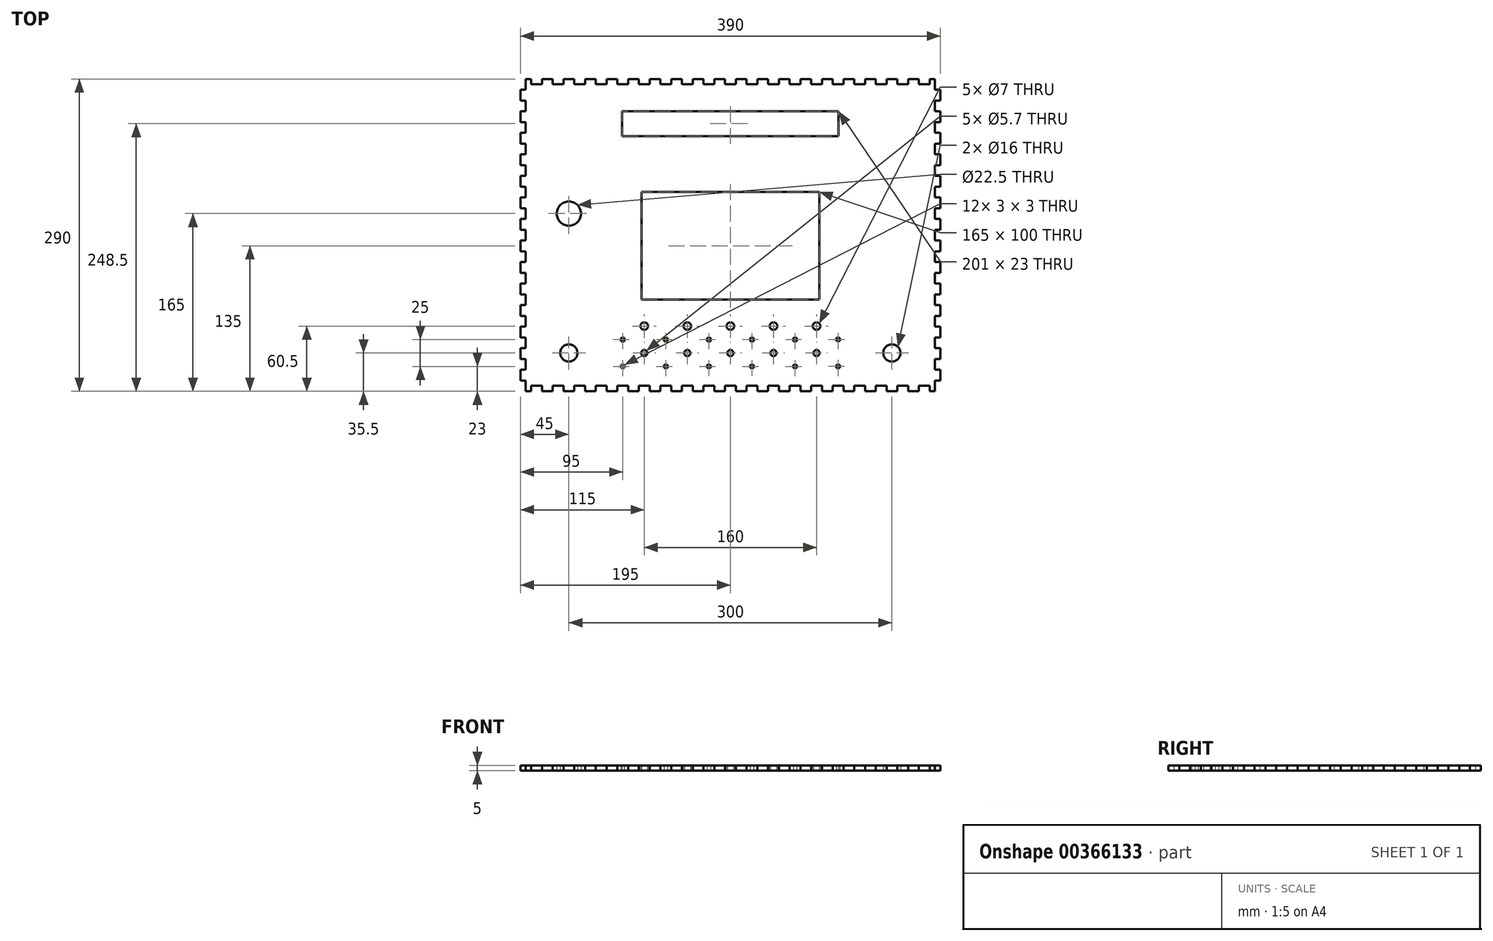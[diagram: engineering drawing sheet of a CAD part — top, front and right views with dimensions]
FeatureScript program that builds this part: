
annotation { "Feature Type Name" : "Feature", "Feature Type Description" : "" }
export const myFeature = defineFeature(function(context is Context, id is Id, definition is map)
    precondition{}
    {
        {
            var Q0;
            Q0=qCreatedBy(makeId("Top.planeOp"),FACE);
            var sketch = newSketch(context, id + "F0", { "sketchPlane" : qUnion([Q0])});
            skPoint(sketch, "E0.middle", {"position": v(0, 0) * mm});
            skLineSegment(sketch, "E1.bottom", {"start": v(82.5, -60) * mm, "end": v(-82.5, -60) * mm});
            skLineSegment(sketch, "E1.top", {"start": v(82.5, 40) * mm, "end": v(-82.5, 40) * mm});
            skLineSegment(sketch, "E1.left", {"start": v(82.5, -60) * mm, "end": v(82.5, 40) * mm});
            skLineSegment(sketch, "E1.right", {"start": v(-82.5, -60) * mm, "end": v(-82.5, 40) * mm});
            skPoint(sketch, "E1.middle", {"position": v(0, -10) * mm});
            skCircle(sketch, "E2", {"center": v(0, -84.5) * mm, "radius": 3.5 * mm});
            skCircle(sketch, "E3", {"center": v(40, -84.5) * mm, "radius": 3.5 * mm});
            skCircle(sketch, "E4", {"center": v(-80, -84.5) * mm, "radius": 3.5 * mm});
            skCircle(sketch, "E5", {"center": v(-40, -84.5) * mm, "radius": 3.5 * mm});
            skCircle(sketch, "E6", {"center": v(80, -84.5) * mm, "radius": 3.5 * mm});
            skLineSegment(sketch, "E7.bottom", {"start": v(100.5, 92) * mm, "end": v(-100.5, 92) * mm});
            skLineSegment(sketch, "E7.top", {"start": v(100.5, 115) * mm, "end": v(-100.5, 115) * mm});
            skLineSegment(sketch, "E7.left", {"start": v(100.5, 92) * mm, "end": v(100.5, 115) * mm});
            skLineSegment(sketch, "E7.right", {"start": v(-100.5, 92) * mm, "end": v(-100.5, 115) * mm});
            skPoint(sketch, "E7.middle", {"position": v(0, 103.5) * mm});
            skCircle(sketch, "E8", {"center": v(0, -109.5) * mm, "radius": 2.85 * mm});
            skCircle(sketch, "E9", {"center": v(-40, -109.5) * mm, "radius": 2.85 * mm});
            skCircle(sketch, "E10", {"center": v(-80, -109.5) * mm, "radius": 2.85 * mm});
            skCircle(sketch, "E11", {"center": v(40, -109.5) * mm, "radius": 2.85 * mm});
            skCircle(sketch, "E12", {"center": v(80, -109.5) * mm, "radius": 2.85 * mm});
            skCircle(sketch, "E13", {"center": v(-150, -109.5) * mm, "radius": 8 * mm});
            skCircle(sketch, "E14", {"center": v(150, -109.5) * mm, "radius": 8 * mm});
            skCircle(sketch, "E15", {"center": v(-150, 20) * mm, "radius": 11.25 * mm});
            skLineSegment(sketch, "E16.bottom", {"start": v(-18.5, -98.5) * mm, "end": v(-21.5, -98.5) * mm});
            skLineSegment(sketch, "E16.top", {"start": v(-18.5, -95.5) * mm, "end": v(-21.5, -95.5) * mm});
            skLineSegment(sketch, "E16.left", {"start": v(-18.5, -98.5) * mm, "end": v(-18.5, -95.5) * mm});
            skLineSegment(sketch, "E16.right", {"start": v(-21.5, -98.5) * mm, "end": v(-21.5, -95.5) * mm});
            skPoint(sketch, "E16.middle", {"position": v(-20, -97) * mm});
            skLineSegment(sketch, "E17.bottom", {"start": v(-58.5, -98.5) * mm, "end": v(-61.5, -98.5) * mm});
            skLineSegment(sketch, "E17.top", {"start": v(-58.5, -95.5) * mm, "end": v(-61.5, -95.5) * mm});
            skLineSegment(sketch, "E17.left", {"start": v(-58.5, -98.5) * mm, "end": v(-58.5, -95.5) * mm});
            skLineSegment(sketch, "E17.right", {"start": v(-61.5, -98.5) * mm, "end": v(-61.5, -95.5) * mm});
            skPoint(sketch, "E17.middle", {"position": v(-60, -97) * mm});
            skLineSegment(sketch, "E18.bottom", {"start": v(-98.5, -98.5) * mm, "end": v(-101.5, -98.5) * mm});
            skLineSegment(sketch, "E18.top", {"start": v(-98.5, -95.5) * mm, "end": v(-101.5, -95.5) * mm});
            skLineSegment(sketch, "E18.left", {"start": v(-98.5, -98.5) * mm, "end": v(-98.5, -95.5) * mm});
            skLineSegment(sketch, "E18.right", {"start": v(-101.5, -98.5) * mm, "end": v(-101.5, -95.5) * mm});
            skPoint(sketch, "E18.middle", {"position": v(-100, -97) * mm});
            skLineSegment(sketch, "E19.bottom", {"start": v(101.5, -98.39) * mm, "end": v(98.5, -98.39) * mm});
            skLineSegment(sketch, "E19.top", {"start": v(101.5, -95.39) * mm, "end": v(98.5, -95.39) * mm});
            skLineSegment(sketch, "E19.left", {"start": v(101.5, -98.39) * mm, "end": v(101.5, -95.39) * mm});
            skLineSegment(sketch, "E19.right", {"start": v(98.5, -98.39) * mm, "end": v(98.5, -95.39) * mm});
            skPoint(sketch, "E19.middle", {"position": v(100, -96.89) * mm});
            skLineSegment(sketch, "E20.bottom", {"start": v(61.5, -98.5) * mm, "end": v(58.5, -98.5) * mm});
            skLineSegment(sketch, "E20.top", {"start": v(61.5, -95.5) * mm, "end": v(58.5, -95.5) * mm});
            skLineSegment(sketch, "E20.left", {"start": v(61.5, -98.5) * mm, "end": v(61.5, -95.5) * mm});
            skLineSegment(sketch, "E20.right", {"start": v(58.5, -98.5) * mm, "end": v(58.5, -95.5) * mm});
            skPoint(sketch, "E20.middle", {"position": v(60, -97) * mm});
            skLineSegment(sketch, "E21.bottom", {"start": v(21.5, -98.5) * mm, "end": v(18.5, -98.5) * mm});
            skLineSegment(sketch, "E21.top", {"start": v(21.5, -95.5) * mm, "end": v(18.5, -95.5) * mm});
            skLineSegment(sketch, "E21.left", {"start": v(21.5, -98.5) * mm, "end": v(21.5, -95.5) * mm});
            skLineSegment(sketch, "E21.right", {"start": v(18.5, -98.5) * mm, "end": v(18.5, -95.5) * mm});
            skPoint(sketch, "E21.middle", {"position": v(20, -97) * mm});
            skPoint(sketch, "E22", {"position": v(-18.5, -97) * mm});
            skLineSegment(sketch, "E23.bottom", {"start": v(-18.5, -123.5) * mm, "end": v(-21.5, -123.5) * mm});
            skLineSegment(sketch, "E23.top", {"start": v(-18.5, -120.5) * mm, "end": v(-21.5, -120.5) * mm});
            skLineSegment(sketch, "E23.left", {"start": v(-18.5, -123.5) * mm, "end": v(-18.5, -120.5) * mm});
            skLineSegment(sketch, "E23.right", {"start": v(-21.5, -123.5) * mm, "end": v(-21.5, -120.5) * mm});
            skPoint(sketch, "E23.middle", {"position": v(-20, -122) * mm});
            skLineSegment(sketch, "E24.bottom", {"start": v(-58.5, -123.5) * mm, "end": v(-61.5, -123.5) * mm});
            skLineSegment(sketch, "E24.top", {"start": v(-58.5, -120.5) * mm, "end": v(-61.5, -120.5) * mm});
            skLineSegment(sketch, "E24.left", {"start": v(-58.5, -123.5) * mm, "end": v(-58.5, -120.5) * mm});
            skLineSegment(sketch, "E24.right", {"start": v(-61.5, -123.5) * mm, "end": v(-61.5, -120.5) * mm});
            skPoint(sketch, "E24.middle", {"position": v(-60, -122) * mm});
            skLineSegment(sketch, "E25.bottom", {"start": v(-98.5, -123.5) * mm, "end": v(-101.5, -123.5) * mm});
            skLineSegment(sketch, "E25.top", {"start": v(-98.5, -120.5) * mm, "end": v(-101.5, -120.5) * mm});
            skLineSegment(sketch, "E25.left", {"start": v(-98.5, -123.5) * mm, "end": v(-98.5, -120.5) * mm});
            skLineSegment(sketch, "E25.right", {"start": v(-101.5, -123.5) * mm, "end": v(-101.5, -120.5) * mm});
            skPoint(sketch, "E25.middle", {"position": v(-100, -122) * mm});
            skLineSegment(sketch, "E26.bottom", {"start": v(101.5, -123.39) * mm, "end": v(98.5, -123.39) * mm});
            skLineSegment(sketch, "E26.top", {"start": v(101.5, -120.39) * mm, "end": v(98.5, -120.39) * mm});
            skLineSegment(sketch, "E26.left", {"start": v(101.5, -123.39) * mm, "end": v(101.5, -120.39) * mm});
            skLineSegment(sketch, "E26.right", {"start": v(98.5, -123.39) * mm, "end": v(98.5, -120.39) * mm});
            skPoint(sketch, "E26.middle", {"position": v(100, -121.89) * mm});
            skLineSegment(sketch, "E27.bottom", {"start": v(61.5, -123.5) * mm, "end": v(58.5, -123.5) * mm});
            skLineSegment(sketch, "E27.top", {"start": v(61.5, -120.5) * mm, "end": v(58.5, -120.5) * mm});
            skLineSegment(sketch, "E27.left", {"start": v(61.5, -123.5) * mm, "end": v(61.5, -120.5) * mm});
            skLineSegment(sketch, "E27.right", {"start": v(58.5, -123.5) * mm, "end": v(58.5, -120.5) * mm});
            skPoint(sketch, "E27.middle", {"position": v(60, -122) * mm});
            skLineSegment(sketch, "E28.bottom", {"start": v(21.5, -123.5) * mm, "end": v(18.5, -123.5) * mm});
            skLineSegment(sketch, "E28.top", {"start": v(21.5, -120.5) * mm, "end": v(18.5, -120.5) * mm});
            skLineSegment(sketch, "E28.left", {"start": v(21.5, -123.5) * mm, "end": v(21.5, -120.5) * mm});
            skLineSegment(sketch, "E28.right", {"start": v(18.5, -123.5) * mm, "end": v(18.5, -120.5) * mm});
            skPoint(sketch, "E28.middle", {"position": v(20, -122) * mm});
            skPoint(sketch, "E29", {"position": v(-18.5, -122) * mm});
            skLineSegment(sketch, "E30", {"start": v(-195, -135) * mm, "end": v(-190, -135) * mm});
            skLineSegment(sketch, "E31", {"start": v(-190, -135) * mm, "end": v(-190, -145) * mm});
            skLineSegment(sketch, "E32", {"start": v(-190, -145) * mm, "end": v(-185, -145) * mm});
            skLineSegment(sketch, "E33", {"start": v(-185, -145) * mm, "end": v(-185, -140) * mm});
            skLineSegment(sketch, "E34", {"start": v(-185, -140) * mm, "end": v(-175, -140) * mm});
            skLineSegment(sketch, "E35", {"start": v(-175, -140) * mm, "end": v(-175, -145) * mm});
            skLineSegment(sketch, "E36", {"start": v(-175, -145) * mm, "end": v(-165, -145) * mm});
            skLineSegment(sketch, "E37", {"start": v(-165, -145) * mm, "end": v(-165, -140) * mm});
            skLineSegment(sketch, "E38", {"start": v(-165, -140) * mm, "end": v(-155, -140) * mm});
            skLineSegment(sketch, "E39", {"start": v(-155, -140) * mm, "end": v(-155, -145) * mm});
            skLineSegment(sketch, "E40.1.0.0", {"start": v(-155, -145) * mm, "end": v(-145, -145) * mm});
            skLineSegment(sketch, "E40.1.0.1", {"start": v(-145, -145) * mm, "end": v(-145, -140) * mm});
            skLineSegment(sketch, "E40.1.0.2", {"start": v(-145, -140) * mm, "end": v(-135, -140) * mm});
            skLineSegment(sketch, "E40.1.0.3", {"start": v(-135, -140) * mm, "end": v(-135, -145) * mm});
            skLineSegment(sketch, "E40.2.0.0", {"start": v(-135, -145) * mm, "end": v(-125, -145) * mm});
            skLineSegment(sketch, "E40.2.0.1", {"start": v(-125, -145) * mm, "end": v(-125, -140) * mm});
            skLineSegment(sketch, "E40.2.0.2", {"start": v(-125, -140) * mm, "end": v(-115, -140) * mm});
            skLineSegment(sketch, "E40.2.0.3", {"start": v(-115, -140) * mm, "end": v(-115, -145) * mm});
            skLineSegment(sketch, "E40.3.0.0", {"start": v(-115, -145) * mm, "end": v(-105, -145) * mm});
            skLineSegment(sketch, "E40.3.0.1", {"start": v(-105, -145) * mm, "end": v(-105, -140) * mm});
            skLineSegment(sketch, "E40.3.0.2", {"start": v(-105, -140) * mm, "end": v(-95, -140) * mm});
            skLineSegment(sketch, "E40.3.0.3", {"start": v(-95, -140) * mm, "end": v(-95, -145) * mm});
            skLineSegment(sketch, "E40.4.0.0", {"start": v(-95, -145) * mm, "end": v(-85, -145) * mm});
            skLineSegment(sketch, "E40.4.0.1", {"start": v(-85, -145) * mm, "end": v(-85, -140) * mm});
            skLineSegment(sketch, "E40.4.0.2", {"start": v(-85, -140) * mm, "end": v(-75, -140) * mm});
            skLineSegment(sketch, "E40.4.0.3", {"start": v(-75, -140) * mm, "end": v(-75, -145) * mm});
            skLineSegment(sketch, "E40.5.0.0", {"start": v(-75, -145) * mm, "end": v(-65, -145) * mm});
            skLineSegment(sketch, "E40.5.0.1", {"start": v(-65, -145) * mm, "end": v(-65, -140) * mm});
            skLineSegment(sketch, "E40.5.0.2", {"start": v(-65, -140) * mm, "end": v(-55, -140) * mm});
            skLineSegment(sketch, "E40.5.0.3", {"start": v(-55, -140) * mm, "end": v(-55, -145) * mm});
            skLineSegment(sketch, "E40.6.0.0", {"start": v(-55, -145) * mm, "end": v(-45, -145) * mm});
            skLineSegment(sketch, "E40.6.0.1", {"start": v(-45, -145) * mm, "end": v(-45, -140) * mm});
            skLineSegment(sketch, "E40.6.0.2", {"start": v(-45, -140) * mm, "end": v(-35, -140) * mm});
            skLineSegment(sketch, "E40.6.0.3", {"start": v(-35, -140) * mm, "end": v(-35, -145) * mm});
            skLineSegment(sketch, "E40.7.0.0", {"start": v(-35, -145) * mm, "end": v(-25, -145) * mm});
            skLineSegment(sketch, "E40.7.0.1", {"start": v(-25, -145) * mm, "end": v(-25, -140) * mm});
            skLineSegment(sketch, "E40.7.0.2", {"start": v(-25, -140) * mm, "end": v(-15, -140) * mm});
            skLineSegment(sketch, "E40.7.0.3", {"start": v(-15, -140) * mm, "end": v(-15, -145) * mm});
            skLineSegment(sketch, "E40.8.0.0", {"start": v(-15, -145) * mm, "end": v(-5, -145) * mm});
            skLineSegment(sketch, "E40.8.0.1", {"start": v(-5, -145) * mm, "end": v(-5, -140) * mm});
            skLineSegment(sketch, "E40.8.0.2", {"start": v(-5, -140) * mm, "end": v(5, -140) * mm});
            skLineSegment(sketch, "E40.8.0.3", {"start": v(5, -140) * mm, "end": v(5, -145) * mm});
            skLineSegment(sketch, "E40.9.0.0", {"start": v(5, -145) * mm, "end": v(15, -145) * mm});
            skLineSegment(sketch, "E40.9.0.1", {"start": v(15, -145) * mm, "end": v(15, -140) * mm});
            skLineSegment(sketch, "E40.9.0.2", {"start": v(15, -140) * mm, "end": v(25, -140) * mm});
            skLineSegment(sketch, "E40.9.0.3", {"start": v(25, -140) * mm, "end": v(25, -145) * mm});
            skLineSegment(sketch, "E40.10.0.0", {"start": v(25, -145) * mm, "end": v(35, -145) * mm});
            skLineSegment(sketch, "E40.10.0.1", {"start": v(35, -145) * mm, "end": v(35, -140) * mm});
            skLineSegment(sketch, "E40.10.0.2", {"start": v(35, -140) * mm, "end": v(45, -140) * mm});
            skLineSegment(sketch, "E40.10.0.3", {"start": v(45, -140) * mm, "end": v(45, -145) * mm});
            skLineSegment(sketch, "E40.11.0.0", {"start": v(45, -145) * mm, "end": v(55, -145) * mm});
            skLineSegment(sketch, "E40.11.0.1", {"start": v(55, -145) * mm, "end": v(55, -140) * mm});
            skLineSegment(sketch, "E40.11.0.2", {"start": v(55, -140) * mm, "end": v(65, -140) * mm});
            skLineSegment(sketch, "E40.11.0.3", {"start": v(65, -140) * mm, "end": v(65, -145) * mm});
            skLineSegment(sketch, "E40.12.0.0", {"start": v(65, -145) * mm, "end": v(75, -145) * mm});
            skLineSegment(sketch, "E40.12.0.1", {"start": v(75, -145) * mm, "end": v(75, -140) * mm});
            skLineSegment(sketch, "E40.12.0.2", {"start": v(75, -140) * mm, "end": v(85, -140) * mm});
            skLineSegment(sketch, "E40.12.0.3", {"start": v(85, -140) * mm, "end": v(85, -145) * mm});
            skLineSegment(sketch, "E40.13.0.0", {"start": v(85, -145) * mm, "end": v(95, -145) * mm});
            skLineSegment(sketch, "E40.13.0.1", {"start": v(95, -145) * mm, "end": v(95, -140) * mm});
            skLineSegment(sketch, "E40.13.0.2", {"start": v(95, -140) * mm, "end": v(105, -140) * mm});
            skLineSegment(sketch, "E40.13.0.3", {"start": v(105, -140) * mm, "end": v(105, -145) * mm});
            skLineSegment(sketch, "E40.14.0.0", {"start": v(105, -145) * mm, "end": v(115, -145) * mm});
            skLineSegment(sketch, "E40.14.0.1", {"start": v(115, -145) * mm, "end": v(115, -140) * mm});
            skLineSegment(sketch, "E40.14.0.2", {"start": v(115, -140) * mm, "end": v(125, -140) * mm});
            skLineSegment(sketch, "E40.14.0.3", {"start": v(125, -140) * mm, "end": v(125, -145) * mm});
            skLineSegment(sketch, "E40.15.0.0", {"start": v(125, -145) * mm, "end": v(135, -145) * mm});
            skLineSegment(sketch, "E40.15.0.1", {"start": v(135, -145) * mm, "end": v(135, -140) * mm});
            skLineSegment(sketch, "E40.15.0.2", {"start": v(135, -140) * mm, "end": v(145, -140) * mm});
            skLineSegment(sketch, "E40.15.0.3", {"start": v(145, -140) * mm, "end": v(145, -145) * mm});
            skLineSegment(sketch, "E40.16.0.0", {"start": v(145, -145) * mm, "end": v(155, -145) * mm});
            skLineSegment(sketch, "E40.16.0.1", {"start": v(155, -145) * mm, "end": v(155, -140) * mm});
            skLineSegment(sketch, "E40.16.0.2", {"start": v(155, -140) * mm, "end": v(165, -140) * mm});
            skLineSegment(sketch, "E40.16.0.3", {"start": v(165, -140) * mm, "end": v(165, -145) * mm});
            skLineSegment(sketch, "E40.17.0.0", {"start": v(165, -145) * mm, "end": v(175, -145) * mm});
            skLineSegment(sketch, "E40.17.0.1", {"start": v(175, -145) * mm, "end": v(175, -140) * mm});
            skLineSegment(sketch, "E40.17.0.2", {"start": v(175, -140) * mm, "end": v(185, -140) * mm});
            skLineSegment(sketch, "E40.17.0.3", {"start": v(185, -140) * mm, "end": v(185, -145) * mm});
            skLineSegment(sketch, "E40.direction1", {"start": v(-175, -145) * mm, "end": v(-155, -145) * mm, "construction": true});
            skLineSegment(sketch, "E41", {"start": v(185, -145) * mm, "end": v(190, -145) * mm});
            skLineSegment(sketch, "E42", {"start": v(190, -145) * mm, "end": v(190, -135) * mm});
            skLineSegment(sketch, "E43", {"start": v(190, -135) * mm, "end": v(195, -135) * mm});
            skLineSegment(sketch, "E44", {"start": v(195, 135) * mm, "end": v(190, 135) * mm});
            skLineSegment(sketch, "E45", {"start": v(190, 135) * mm, "end": v(190, 145) * mm});
            skLineSegment(sketch, "E46", {"start": v(190, 145) * mm, "end": v(185, 145) * mm});
            skLineSegment(sketch, "E47", {"start": v(185, 145) * mm, "end": v(185, 140) * mm});
            skLineSegment(sketch, "E48", {"start": v(185, 140) * mm, "end": v(175, 140) * mm});
            skLineSegment(sketch, "E49", {"start": v(175, 140) * mm, "end": v(175, 145) * mm});
            skLineSegment(sketch, "E50", {"start": v(175, 145) * mm, "end": v(165, 145) * mm});
            skLineSegment(sketch, "E51", {"start": v(165, 145) * mm, "end": v(165, 140) * mm});
            skLineSegment(sketch, "E52", {"start": v(165, 140) * mm, "end": v(155, 140) * mm});
            skLineSegment(sketch, "E53", {"start": v(155, 140) * mm, "end": v(155, 145) * mm});
            skLineSegment(sketch, "E54.1.0.0", {"start": v(155, 145) * mm, "end": v(145, 145) * mm});
            skLineSegment(sketch, "E54.1.0.1", {"start": v(145, 145) * mm, "end": v(145, 140) * mm});
            skLineSegment(sketch, "E54.1.0.2", {"start": v(145, 140) * mm, "end": v(135, 140) * mm});
            skLineSegment(sketch, "E54.1.0.3", {"start": v(135, 140) * mm, "end": v(135, 145) * mm});
            skLineSegment(sketch, "E54.2.0.0", {"start": v(135, 145) * mm, "end": v(125, 145) * mm});
            skLineSegment(sketch, "E54.2.0.1", {"start": v(125, 145) * mm, "end": v(125, 140) * mm});
            skLineSegment(sketch, "E54.2.0.2", {"start": v(125, 140) * mm, "end": v(115, 140) * mm});
            skLineSegment(sketch, "E54.2.0.3", {"start": v(115, 140) * mm, "end": v(115, 145) * mm});
            skLineSegment(sketch, "E54.3.0.0", {"start": v(115, 145) * mm, "end": v(105, 145) * mm});
            skLineSegment(sketch, "E54.3.0.1", {"start": v(105, 145) * mm, "end": v(105, 140) * mm});
            skLineSegment(sketch, "E54.3.0.2", {"start": v(105, 140) * mm, "end": v(95, 140) * mm});
            skLineSegment(sketch, "E54.3.0.3", {"start": v(95, 140) * mm, "end": v(95, 145) * mm});
            skLineSegment(sketch, "E54.4.0.0", {"start": v(95, 145) * mm, "end": v(85, 145) * mm});
            skLineSegment(sketch, "E54.4.0.1", {"start": v(85, 145) * mm, "end": v(85, 140) * mm});
            skLineSegment(sketch, "E54.4.0.2", {"start": v(85, 140) * mm, "end": v(75, 140) * mm});
            skLineSegment(sketch, "E54.4.0.3", {"start": v(75, 140) * mm, "end": v(75, 145) * mm});
            skLineSegment(sketch, "E54.5.0.0", {"start": v(75, 145) * mm, "end": v(65, 145) * mm});
            skLineSegment(sketch, "E54.5.0.1", {"start": v(65, 145) * mm, "end": v(65, 140) * mm});
            skLineSegment(sketch, "E54.5.0.2", {"start": v(65, 140) * mm, "end": v(55, 140) * mm});
            skLineSegment(sketch, "E54.5.0.3", {"start": v(55, 140) * mm, "end": v(55, 145) * mm});
            skLineSegment(sketch, "E54.6.0.0", {"start": v(55, 145) * mm, "end": v(45, 145) * mm});
            skLineSegment(sketch, "E54.6.0.1", {"start": v(45, 145) * mm, "end": v(45, 140) * mm});
            skLineSegment(sketch, "E54.6.0.2", {"start": v(45, 140) * mm, "end": v(35, 140) * mm});
            skLineSegment(sketch, "E54.6.0.3", {"start": v(35, 140) * mm, "end": v(35, 145) * mm});
            skLineSegment(sketch, "E54.7.0.0", {"start": v(35, 145) * mm, "end": v(25, 145) * mm});
            skLineSegment(sketch, "E54.7.0.1", {"start": v(25, 145) * mm, "end": v(25, 140) * mm});
            skLineSegment(sketch, "E54.7.0.2", {"start": v(25, 140) * mm, "end": v(15, 140) * mm});
            skLineSegment(sketch, "E54.7.0.3", {"start": v(15, 140) * mm, "end": v(15, 145) * mm});
            skLineSegment(sketch, "E54.8.0.0", {"start": v(15, 145) * mm, "end": v(5, 145) * mm});
            skLineSegment(sketch, "E54.8.0.1", {"start": v(5, 145) * mm, "end": v(5, 140) * mm});
            skLineSegment(sketch, "E54.8.0.2", {"start": v(5, 140) * mm, "end": v(-5, 140) * mm});
            skLineSegment(sketch, "E54.8.0.3", {"start": v(-5, 140) * mm, "end": v(-5, 145) * mm});
            skLineSegment(sketch, "E54.9.0.0", {"start": v(-5, 145) * mm, "end": v(-15, 145) * mm});
            skLineSegment(sketch, "E54.9.0.1", {"start": v(-15, 145) * mm, "end": v(-15, 140) * mm});
            skLineSegment(sketch, "E54.9.0.2", {"start": v(-15, 140) * mm, "end": v(-25, 140) * mm});
            skLineSegment(sketch, "E54.9.0.3", {"start": v(-25, 140) * mm, "end": v(-25, 145) * mm});
            skLineSegment(sketch, "E54.10.0.0", {"start": v(-25, 145) * mm, "end": v(-35, 145) * mm});
            skLineSegment(sketch, "E54.10.0.1", {"start": v(-35, 145) * mm, "end": v(-35, 140) * mm});
            skLineSegment(sketch, "E54.10.0.2", {"start": v(-35, 140) * mm, "end": v(-45, 140) * mm});
            skLineSegment(sketch, "E54.10.0.3", {"start": v(-45, 140) * mm, "end": v(-45, 145) * mm});
            skLineSegment(sketch, "E54.11.0.0", {"start": v(-45, 145) * mm, "end": v(-55, 145) * mm});
            skLineSegment(sketch, "E54.11.0.1", {"start": v(-55, 145) * mm, "end": v(-55, 140) * mm});
            skLineSegment(sketch, "E54.11.0.2", {"start": v(-55, 140) * mm, "end": v(-65, 140) * mm});
            skLineSegment(sketch, "E54.11.0.3", {"start": v(-65, 140) * mm, "end": v(-65, 145) * mm});
            skLineSegment(sketch, "E54.12.0.0", {"start": v(-65, 145) * mm, "end": v(-75, 145) * mm});
            skLineSegment(sketch, "E54.12.0.1", {"start": v(-75, 145) * mm, "end": v(-75, 140) * mm});
            skLineSegment(sketch, "E54.12.0.2", {"start": v(-75, 140) * mm, "end": v(-85, 140) * mm});
            skLineSegment(sketch, "E54.12.0.3", {"start": v(-85, 140) * mm, "end": v(-85, 145) * mm});
            skLineSegment(sketch, "E54.13.0.0", {"start": v(-85, 145) * mm, "end": v(-95, 145) * mm});
            skLineSegment(sketch, "E54.13.0.1", {"start": v(-95, 145) * mm, "end": v(-95, 140) * mm});
            skLineSegment(sketch, "E54.13.0.2", {"start": v(-95, 140) * mm, "end": v(-105, 140) * mm});
            skLineSegment(sketch, "E54.13.0.3", {"start": v(-105, 140) * mm, "end": v(-105, 145) * mm});
            skLineSegment(sketch, "E54.14.0.0", {"start": v(-105, 145) * mm, "end": v(-115, 145) * mm});
            skLineSegment(sketch, "E54.14.0.1", {"start": v(-115, 145) * mm, "end": v(-115, 140) * mm});
            skLineSegment(sketch, "E54.14.0.2", {"start": v(-115, 140) * mm, "end": v(-125, 140) * mm});
            skLineSegment(sketch, "E54.14.0.3", {"start": v(-125, 140) * mm, "end": v(-125, 145) * mm});
            skLineSegment(sketch, "E54.15.0.0", {"start": v(-125, 145) * mm, "end": v(-135, 145) * mm});
            skLineSegment(sketch, "E54.15.0.1", {"start": v(-135, 145) * mm, "end": v(-135, 140) * mm});
            skLineSegment(sketch, "E54.15.0.2", {"start": v(-135, 140) * mm, "end": v(-145, 140) * mm});
            skLineSegment(sketch, "E54.15.0.3", {"start": v(-145, 140) * mm, "end": v(-145, 145) * mm});
            skLineSegment(sketch, "E54.16.0.0", {"start": v(-145, 145) * mm, "end": v(-155, 145) * mm});
            skLineSegment(sketch, "E54.16.0.1", {"start": v(-155, 145) * mm, "end": v(-155, 140) * mm});
            skLineSegment(sketch, "E54.16.0.2", {"start": v(-155, 140) * mm, "end": v(-165, 140) * mm});
            skLineSegment(sketch, "E54.16.0.3", {"start": v(-165, 140) * mm, "end": v(-165, 145) * mm});
            skLineSegment(sketch, "E54.17.0.0", {"start": v(-165, 145) * mm, "end": v(-175, 145) * mm});
            skLineSegment(sketch, "E54.17.0.1", {"start": v(-175, 145) * mm, "end": v(-175, 140) * mm});
            skLineSegment(sketch, "E54.17.0.2", {"start": v(-175, 140) * mm, "end": v(-185, 140) * mm});
            skLineSegment(sketch, "E54.17.0.3", {"start": v(-185, 140) * mm, "end": v(-185, 145) * mm});
            skLineSegment(sketch, "E54.direction1", {"start": v(175, 145) * mm, "end": v(155, 145) * mm, "construction": true});
            skLineSegment(sketch, "E55", {"start": v(-185, 145) * mm, "end": v(-190, 145) * mm});
            skLineSegment(sketch, "E56", {"start": v(-190, 145) * mm, "end": v(-190, 135) * mm});
            skLineSegment(sketch, "E57", {"start": v(-190, 135) * mm, "end": v(-195, 135) * mm});
            skLineSegment(sketch, "E58", {"start": v(-195, 135) * mm, "end": v(-195, 125) * mm});
            skLineSegment(sketch, "E59", {"start": v(-195, 125) * mm, "end": v(-190, 125) * mm});
            skLineSegment(sketch, "E60", {"start": v(-190, 125) * mm, "end": v(-190, 115) * mm});
            skLineSegment(sketch, "E61.1.0.0", {"start": v(-190, 115) * mm, "end": v(-195, 115) * mm});
            skLineSegment(sketch, "E61.1.0.1", {"start": v(-195, 115) * mm, "end": v(-195, 105) * mm});
            skLineSegment(sketch, "E61.1.0.2", {"start": v(-195, 105) * mm, "end": v(-190, 105) * mm});
            skLineSegment(sketch, "E61.1.0.3", {"start": v(-190, 105) * mm, "end": v(-190, 95) * mm});
            skLineSegment(sketch, "E61.2.0.0", {"start": v(-190, 95) * mm, "end": v(-195, 95) * mm});
            skLineSegment(sketch, "E61.2.0.1", {"start": v(-195, 95) * mm, "end": v(-195, 85) * mm});
            skLineSegment(sketch, "E61.2.0.2", {"start": v(-195, 85) * mm, "end": v(-190, 85) * mm});
            skLineSegment(sketch, "E61.2.0.3", {"start": v(-190, 85) * mm, "end": v(-190, 75) * mm});
            skLineSegment(sketch, "E61.3.0.0", {"start": v(-190, 75) * mm, "end": v(-195, 75) * mm});
            skLineSegment(sketch, "E61.3.0.1", {"start": v(-195, 75) * mm, "end": v(-195, 65) * mm});
            skLineSegment(sketch, "E61.3.0.2", {"start": v(-195, 65) * mm, "end": v(-190, 65) * mm});
            skLineSegment(sketch, "E61.3.0.3", {"start": v(-190, 65) * mm, "end": v(-190, 55) * mm});
            skLineSegment(sketch, "E61.4.0.0", {"start": v(-190, 55) * mm, "end": v(-195, 55) * mm});
            skLineSegment(sketch, "E61.4.0.1", {"start": v(-195, 55) * mm, "end": v(-195, 45) * mm});
            skLineSegment(sketch, "E61.4.0.2", {"start": v(-195, 45) * mm, "end": v(-190, 45) * mm});
            skLineSegment(sketch, "E61.4.0.3", {"start": v(-190, 45) * mm, "end": v(-190, 35) * mm});
            skLineSegment(sketch, "E61.5.0.0", {"start": v(-190, 35) * mm, "end": v(-195, 35) * mm});
            skLineSegment(sketch, "E61.5.0.1", {"start": v(-195, 35) * mm, "end": v(-195, 25) * mm});
            skLineSegment(sketch, "E61.5.0.2", {"start": v(-195, 25) * mm, "end": v(-190, 25) * mm});
            skLineSegment(sketch, "E61.5.0.3", {"start": v(-190, 25) * mm, "end": v(-190, 15) * mm});
            skLineSegment(sketch, "E61.6.0.0", {"start": v(-190, 15) * mm, "end": v(-195, 15) * mm});
            skLineSegment(sketch, "E61.6.0.1", {"start": v(-195, 15) * mm, "end": v(-195, 5) * mm});
            skLineSegment(sketch, "E61.6.0.2", {"start": v(-195, 5) * mm, "end": v(-190, 5) * mm});
            skLineSegment(sketch, "E61.6.0.3", {"start": v(-190, 5) * mm, "end": v(-190, -5) * mm});
            skLineSegment(sketch, "E61.7.0.0", {"start": v(-190, -5) * mm, "end": v(-195, -5) * mm});
            skLineSegment(sketch, "E61.7.0.1", {"start": v(-195, -5) * mm, "end": v(-195, -15) * mm});
            skLineSegment(sketch, "E61.7.0.2", {"start": v(-195, -15) * mm, "end": v(-190, -15) * mm});
            skLineSegment(sketch, "E61.7.0.3", {"start": v(-190, -15) * mm, "end": v(-190, -25) * mm});
            skLineSegment(sketch, "E61.8.0.0", {"start": v(-190, -25) * mm, "end": v(-195, -25) * mm});
            skLineSegment(sketch, "E61.8.0.1", {"start": v(-195, -25) * mm, "end": v(-195, -35) * mm});
            skLineSegment(sketch, "E61.8.0.2", {"start": v(-195, -35) * mm, "end": v(-190, -35) * mm});
            skLineSegment(sketch, "E61.8.0.3", {"start": v(-190, -35) * mm, "end": v(-190, -45) * mm});
            skLineSegment(sketch, "E61.9.0.0", {"start": v(-190, -45) * mm, "end": v(-195, -45) * mm});
            skLineSegment(sketch, "E61.9.0.1", {"start": v(-195, -45) * mm, "end": v(-195, -55) * mm});
            skLineSegment(sketch, "E61.9.0.2", {"start": v(-195, -55) * mm, "end": v(-190, -55) * mm});
            skLineSegment(sketch, "E61.9.0.3", {"start": v(-190, -55) * mm, "end": v(-190, -65) * mm});
            skLineSegment(sketch, "E61.10.0.0", {"start": v(-190, -65) * mm, "end": v(-195, -65) * mm});
            skLineSegment(sketch, "E61.10.0.1", {"start": v(-195, -65) * mm, "end": v(-195, -75) * mm});
            skLineSegment(sketch, "E61.10.0.2", {"start": v(-195, -75) * mm, "end": v(-190, -75) * mm});
            skLineSegment(sketch, "E61.10.0.3", {"start": v(-190, -75) * mm, "end": v(-190, -85) * mm});
            skLineSegment(sketch, "E61.11.0.0", {"start": v(-190, -85) * mm, "end": v(-195, -85) * mm});
            skLineSegment(sketch, "E61.11.0.1", {"start": v(-195, -85) * mm, "end": v(-195, -95) * mm});
            skLineSegment(sketch, "E61.11.0.2", {"start": v(-195, -95) * mm, "end": v(-190, -95) * mm});
            skLineSegment(sketch, "E61.11.0.3", {"start": v(-190, -95) * mm, "end": v(-190, -105) * mm});
            skLineSegment(sketch, "E61.12.0.0", {"start": v(-190, -105) * mm, "end": v(-195, -105) * mm});
            skLineSegment(sketch, "E61.12.0.1", {"start": v(-195, -105) * mm, "end": v(-195, -115) * mm});
            skLineSegment(sketch, "E61.12.0.2", {"start": v(-195, -115) * mm, "end": v(-190, -115) * mm});
            skLineSegment(sketch, "E61.12.0.3", {"start": v(-190, -115) * mm, "end": v(-190, -125) * mm});
            skLineSegment(sketch, "E61.13.0.0", {"start": v(-190, -125) * mm, "end": v(-195, -125) * mm});
            skLineSegment(sketch, "E61.13.0.1", {"start": v(-195, -125) * mm, "end": v(-195, -135) * mm});
            skLineSegment(sketch, "E62", {"start": v(195, -135) * mm, "end": v(195, -125) * mm});
            skLineSegment(sketch, "E63", {"start": v(195, -125) * mm, "end": v(190, -125) * mm});
            skLineSegment(sketch, "E64", {"start": v(190, -125) * mm, "end": v(190, -115) * mm});
            skLineSegment(sketch, "E65.1.0.0", {"start": v(190, -115) * mm, "end": v(195, -115) * mm});
            skLineSegment(sketch, "E65.1.0.1", {"start": v(195, -115) * mm, "end": v(195, -105) * mm});
            skLineSegment(sketch, "E65.1.0.2", {"start": v(195, -105) * mm, "end": v(190, -105) * mm});
            skLineSegment(sketch, "E65.1.0.3", {"start": v(190, -105) * mm, "end": v(190, -95) * mm});
            skLineSegment(sketch, "E65.2.0.0", {"start": v(190, -95) * mm, "end": v(195, -95) * mm});
            skLineSegment(sketch, "E65.2.0.1", {"start": v(195, -95) * mm, "end": v(195, -85) * mm});
            skLineSegment(sketch, "E65.2.0.2", {"start": v(195, -85) * mm, "end": v(190, -85) * mm});
            skLineSegment(sketch, "E65.2.0.3", {"start": v(190, -85) * mm, "end": v(190, -75) * mm});
            skLineSegment(sketch, "E65.3.0.0", {"start": v(190, -75) * mm, "end": v(195, -75) * mm});
            skLineSegment(sketch, "E65.3.0.1", {"start": v(195, -75) * mm, "end": v(195, -65) * mm});
            skLineSegment(sketch, "E65.3.0.2", {"start": v(195, -65) * mm, "end": v(190, -65) * mm});
            skLineSegment(sketch, "E65.3.0.3", {"start": v(190, -65) * mm, "end": v(190, -55) * mm});
            skLineSegment(sketch, "E65.4.0.0", {"start": v(190, -55) * mm, "end": v(195, -55) * mm});
            skLineSegment(sketch, "E65.4.0.1", {"start": v(195, -55) * mm, "end": v(195, -45) * mm});
            skLineSegment(sketch, "E65.4.0.2", {"start": v(195, -45) * mm, "end": v(190, -45) * mm});
            skLineSegment(sketch, "E65.4.0.3", {"start": v(190, -45) * mm, "end": v(190, -35) * mm});
            skLineSegment(sketch, "E65.5.0.0", {"start": v(190, -35) * mm, "end": v(195, -35) * mm});
            skLineSegment(sketch, "E65.5.0.1", {"start": v(195, -35) * mm, "end": v(195, -25) * mm});
            skLineSegment(sketch, "E65.5.0.2", {"start": v(195, -25) * mm, "end": v(190, -25) * mm});
            skLineSegment(sketch, "E65.5.0.3", {"start": v(190, -25) * mm, "end": v(190, -15) * mm});
            skLineSegment(sketch, "E65.6.0.0", {"start": v(190, -15) * mm, "end": v(195, -15) * mm});
            skLineSegment(sketch, "E65.6.0.1", {"start": v(195, -15) * mm, "end": v(195, -5) * mm});
            skLineSegment(sketch, "E65.6.0.2", {"start": v(195, -5) * mm, "end": v(190, -5) * mm});
            skLineSegment(sketch, "E65.6.0.3", {"start": v(190, -5) * mm, "end": v(190, 5) * mm});
            skLineSegment(sketch, "E65.7.0.0", {"start": v(190, 5) * mm, "end": v(195, 5) * mm});
            skLineSegment(sketch, "E65.7.0.1", {"start": v(195, 5) * mm, "end": v(195, 15) * mm});
            skLineSegment(sketch, "E65.7.0.2", {"start": v(195, 15) * mm, "end": v(190, 15) * mm});
            skLineSegment(sketch, "E65.7.0.3", {"start": v(190, 15) * mm, "end": v(190, 25) * mm});
            skLineSegment(sketch, "E65.8.0.0", {"start": v(190, 25) * mm, "end": v(195, 25) * mm});
            skLineSegment(sketch, "E65.8.0.1", {"start": v(195, 25) * mm, "end": v(195, 35) * mm});
            skLineSegment(sketch, "E65.8.0.2", {"start": v(195, 35) * mm, "end": v(190, 35) * mm});
            skLineSegment(sketch, "E65.8.0.3", {"start": v(190, 35) * mm, "end": v(190, 45) * mm});
            skLineSegment(sketch, "E65.9.0.0", {"start": v(190, 45) * mm, "end": v(195, 45) * mm});
            skLineSegment(sketch, "E65.9.0.1", {"start": v(195, 45) * mm, "end": v(195, 55) * mm});
            skLineSegment(sketch, "E65.9.0.2", {"start": v(195, 55) * mm, "end": v(190, 55) * mm});
            skLineSegment(sketch, "E65.9.0.3", {"start": v(190, 55) * mm, "end": v(190, 65) * mm});
            skLineSegment(sketch, "E65.10.0.0", {"start": v(190, 65) * mm, "end": v(195, 65) * mm});
            skLineSegment(sketch, "E65.10.0.1", {"start": v(195, 65) * mm, "end": v(195, 75) * mm});
            skLineSegment(sketch, "E65.10.0.2", {"start": v(195, 75) * mm, "end": v(190, 75) * mm});
            skLineSegment(sketch, "E65.10.0.3", {"start": v(190, 75) * mm, "end": v(190, 85) * mm});
            skLineSegment(sketch, "E65.11.0.0", {"start": v(190, 85) * mm, "end": v(195, 85) * mm});
            skLineSegment(sketch, "E65.11.0.1", {"start": v(195, 85) * mm, "end": v(195, 95) * mm});
            skLineSegment(sketch, "E65.11.0.2", {"start": v(195, 95) * mm, "end": v(190, 95) * mm});
            skLineSegment(sketch, "E65.11.0.3", {"start": v(190, 95) * mm, "end": v(190, 105) * mm});
            skLineSegment(sketch, "E65.12.0.0", {"start": v(190, 105) * mm, "end": v(195, 105) * mm});
            skLineSegment(sketch, "E65.12.0.1", {"start": v(195, 105) * mm, "end": v(195, 115) * mm});
            skLineSegment(sketch, "E65.12.0.2", {"start": v(195, 115) * mm, "end": v(190, 115) * mm});
            skLineSegment(sketch, "E65.12.0.3", {"start": v(190, 115) * mm, "end": v(190, 125) * mm});
            skLineSegment(sketch, "E65.13.0.0", {"start": v(190, 125) * mm, "end": v(195, 125) * mm});
            skLineSegment(sketch, "E65.13.0.1", {"start": v(195, 125) * mm, "end": v(195, 135) * mm});
            skSolve(sketch);
        }
        {
            var Q0;
            Q0 = qSketchRegion(id + "F0", true);
            extrude(context, id + "F1", {"entities" : qUnion([Q0]), "endBound" : BoundingType.SYMMETRIC, "depth" : 5 * mm});
        }
    });
